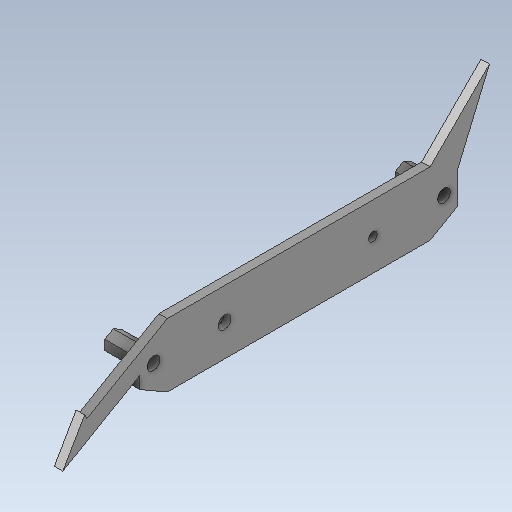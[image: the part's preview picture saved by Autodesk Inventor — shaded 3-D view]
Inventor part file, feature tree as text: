
AUTODESK INVENTOR PART (.ipt)
format: ipt  version: 2020 (Build 240168000, 168)  size: 165,888 bytes
history: native  units: in
note: dims shown in document units (in); Inventor stores cm internally (conversion verified against a paired STEP export)
features: other x3, extrude x2, sketch x2
ambient origin geometry x8: Origin, YZ Plane, XZ Plane, XY Plane, X Axis, Y Axis, Z Axis, Center Point
bodies: Solid1 (feature_tree)
feature tree (7):
  other  "HexWheelGuard.ipt"
  extrude  "Extrusion1"  Depth=0.315in
  extrude  "Extrusion2"  Depth=0.3937in
  other  "Solid1::HexWheelGuard.ipt"
  other  "TaggingFeature2"
  sketch  "Sketch1"  dims[d1=0.3937in d2=0.315in]
  sketch  "Sketch2"  dims[d3=60.0deg d4=1.4843in d5=0.0787in d6=0.3937in d7=0.0in d10=0.5906in d11=1.1024in d12=0.3937in d13=0.0in]
